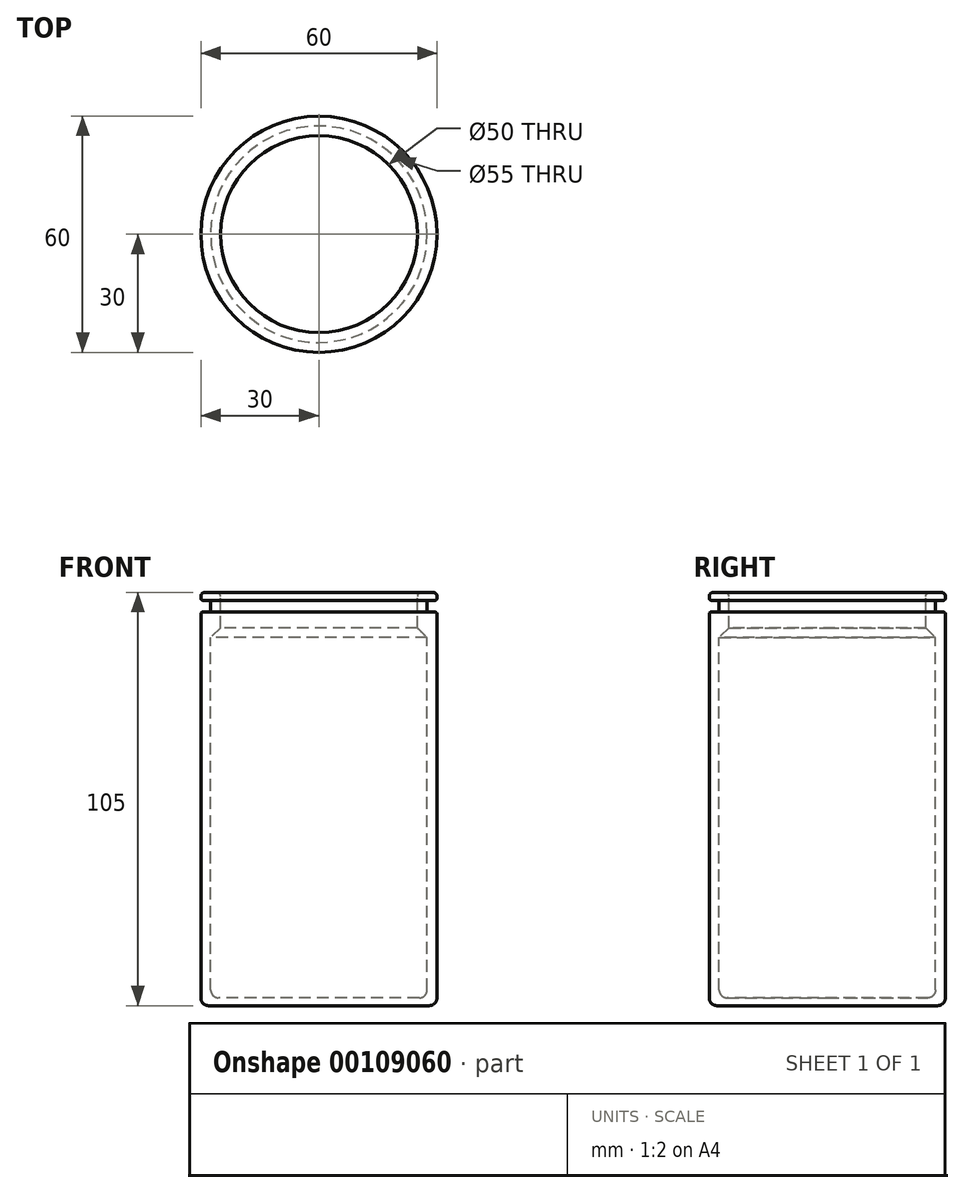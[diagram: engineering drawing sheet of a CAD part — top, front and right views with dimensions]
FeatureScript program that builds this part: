
annotation { "Feature Type Name" : "Feature", "Feature Type Description" : "" }
export const myFeature = defineFeature(function(context is Context, id is Id, definition is map)
    precondition{}
    {
        {
            var Q0;
            Q0=qCreatedBy(makeId("Front.planeOp"),FACE);
            var sketch = newSketch(context, id + "F0", { "sketchPlane" : qUnion([Q0])});
            skLineSegment(sketch, "E0", {"start": v(0, -15.62) * mm, "end": v(0, -17.62) * mm});
            skLineSegment(sketch, "E1", {"start": v(0, -17.62) * mm, "end": v(28, -17.62) * mm});
            skLineSegment(sketch, "E2", {"start": v(30, -15.62) * mm, "end": v(30, 81.88) * mm});
            skLineSegment(sketch, "E3", {"start": v(29.5, 82.38) * mm, "end": v(28, 82.38) * mm});
            skLineSegment(sketch, "E4", {"start": v(27.5, 82.88) * mm, "end": v(27.5, 84.88) * mm});
            skLineSegment(sketch, "E5", {"start": v(28, 85.38) * mm, "end": v(29.5, 85.38) * mm});
            skLineSegment(sketch, "E6", {"start": v(30, 85.88) * mm, "end": v(30, 86.38) * mm});
            skLineSegment(sketch, "E7", {"start": v(29, 87.38) * mm, "end": v(26, 87.38) * mm});
            skLineSegment(sketch, "E8", {"start": v(25, 86.38) * mm, "end": v(25, 78.38) * mm});
            skLineSegment(sketch, "E9", {"start": v(26, 77.38) * mm, "end": v(26, 77.38) * mm});
            skLineSegment(sketch, "E10", {"start": v(27.5, 75.88) * mm, "end": v(27.5, -13.62) * mm});
            skLineSegment(sketch, "E11", {"start": v(25.5, -15.62) * mm, "end": v(0, -15.62) * mm});
            skPoint(sketch, "E12.visualSharp", {"position": v(27.5, 77.38) * mm});
            skPoint(sketch, "E13.visualSharp", {"position": v(27.5, -15.62) * mm});
            skArc(sketch, "E13.filletArc", {"start": v(25.5, -15.62) * mm, "mid": v(26.91, -15.04) * mm, "end": v(27.5, -13.62) * mm});
            skPoint(sketch, "E14.visualSharp", {"position": v(30, -17.62) * mm});
            skArc(sketch, "E14.filletArc", {"start": v(28, -17.62) * mm, "mid": v(29.41, -17.04) * mm, "end": v(30, -15.62) * mm});
            skPoint(sketch, "E15.visualSharp", {"position": v(30, 87.38) * mm});
            skArc(sketch, "E15.filletArc", {"start": v(30, 86.38) * mm, "mid": v(29.7, 87.09) * mm, "end": v(29, 87.38) * mm});
            skPoint(sketch, "E16.visualSharp", {"position": v(25, 87.38) * mm});
            skArc(sketch, "E16.filletArc", {"start": v(26, 87.38) * mm, "mid": v(25.3, 87.09) * mm, "end": v(25, 86.38) * mm});
            skPoint(sketch, "E17.visualSharp", {"position": v(30, 85.38) * mm});
            skArc(sketch, "E17.filletArc", {"start": v(29.5, 85.38) * mm, "mid": v(29.85, 85.52) * mm, "end": v(30, 85.88) * mm});
            skPoint(sketch, "E18.visualSharp", {"position": v(27.5, 85.38) * mm});
            skArc(sketch, "E18.filletArc", {"start": v(28, 85.38) * mm, "mid": v(27.65, 85.23) * mm, "end": v(27.5, 84.88) * mm});
            skPoint(sketch, "E19.visualSharp", {"position": v(27.5, 82.38) * mm});
            skArc(sketch, "E19.filletArc", {"start": v(27.5, 82.88) * mm, "mid": v(27.65, 82.52) * mm, "end": v(28, 82.38) * mm});
            skPoint(sketch, "E20.visualSharp", {"position": v(30, 82.38) * mm});
            skArc(sketch, "E20.filletArc", {"start": v(30, 81.88) * mm, "mid": v(29.85, 82.23) * mm, "end": v(29.5, 82.38) * mm});
            skPoint(sketch, "E21.visualSharp", {"position": v(25, 77.38) * mm});
            skLineSegment(sketch, "E22", {"start": v(25, 78.38) * mm, "end": v(27.5, 75.88) * mm});
            skSolve(sketch);
        }
        {
            var Q0;
            Q0=makeQuery(id+"F0.imprint","IMPRINT",FACE,{"disambiguationData":[TD([[makeQuery(id+"F0.imprint","IMPRINT",EDGE,{"derivedFrom":sQuery(id+"F0.wireOp",EDGE,"E0")}),1.0]])]});
            var Q1;
            Q1=sQuery(id+"F0.wireOp",EDGE,"E0");
            revolve(context, id + "F1", {"entities" : qUnion([Q0]), "axis" : qUnion([Q1]), "revolveType" : RevolveType.FULL});
        }
    });
